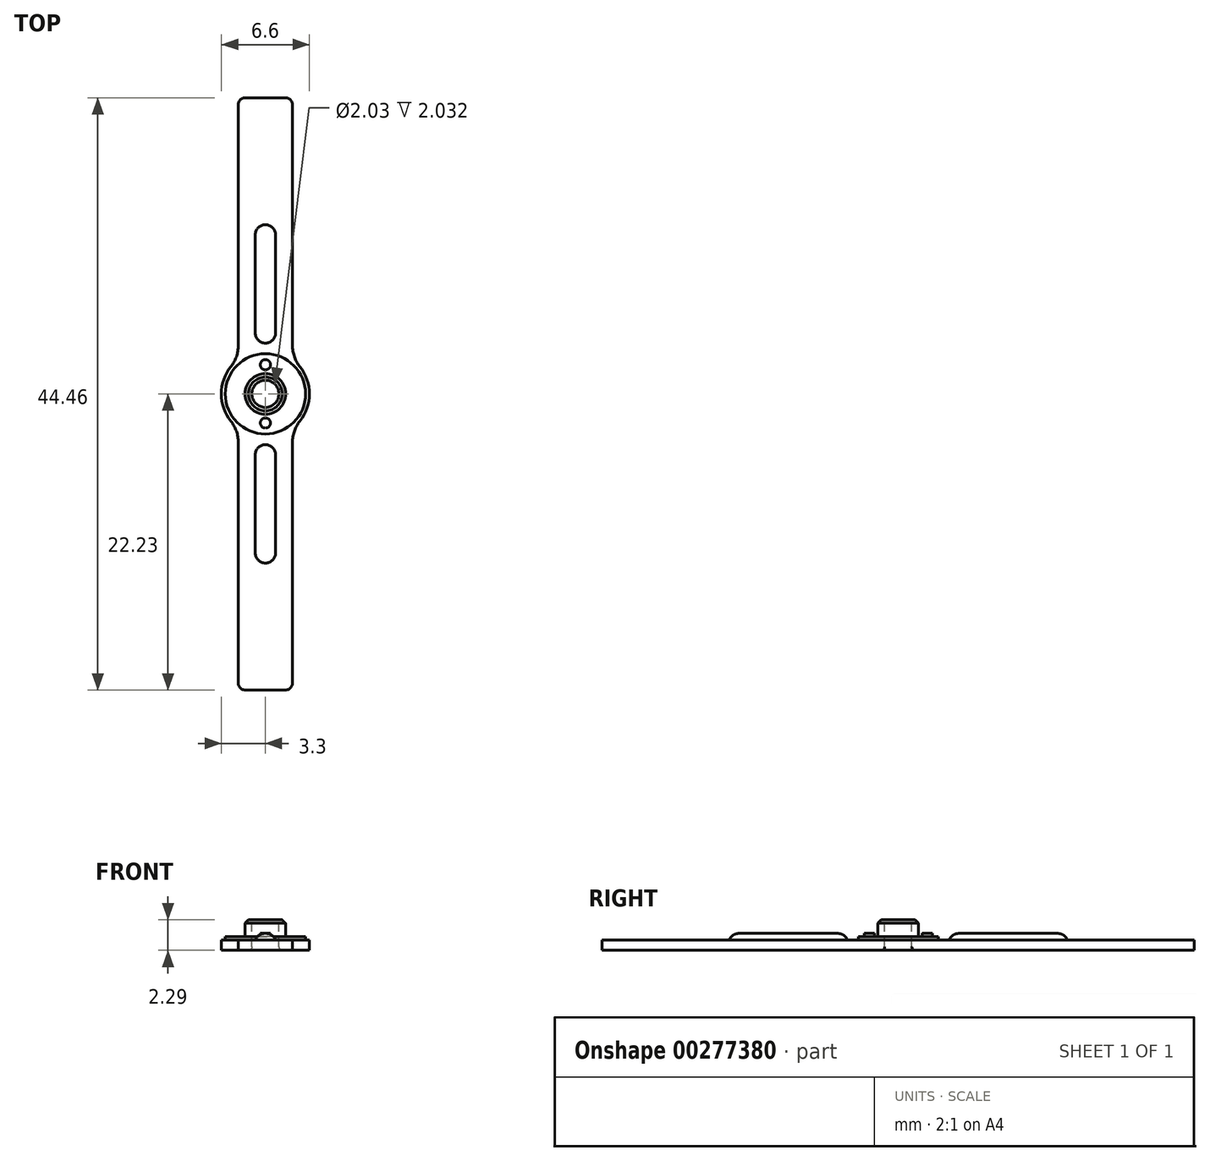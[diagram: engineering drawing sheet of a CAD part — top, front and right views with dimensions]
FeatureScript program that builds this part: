
annotation { "Feature Type Name" : "Feature", "Feature Type Description" : "" }
export const myFeature = defineFeature(function(context is Context, id is Id, definition is map)
    precondition{}
    {
        {
            var Q0;
            Q0=qCreatedBy(makeId("Top.planeOp"),FACE);
            var sketch = newSketch(context, id + "F0", { "sketchPlane" : qUnion([Q0])});
            skArc(sketch, "E0", {"start": v(2.03, -2.6) * mm, "mid": v(3.3, 0) * mm, "end": v(2.03, 2.6) * mm});
            skLineSegment(sketch, "E1", {"start": v(-2.03, 14.6) * mm, "end": v(-2.03, 2.6) * mm});
            skLineSegment(sketch, "E2", {"start": v(2.03, 14.6) * mm, "end": v(2.03, 2.6) * mm});
            skLineSegment(sketch, "E3", {"start": v(-2.03, 22.22) * mm, "end": v(2.03, 22.22) * mm});
            skLineSegment(sketch, "E4", {"start": v(-2.03, -22.23) * mm, "end": v(2.03, -22.22) * mm});
            skPoint(sketch, "E5.orphan", {"position": v(-2.03, -22.23) * mm});
            skPoint(sketch, "E6.orphan", {"position": v(2.03, -22.22) * mm});
            skArc(sketch, "E7.trimOffspring", {"start": v(-2.03, 2.6) * mm, "mid": v(-3.3, 0) * mm, "end": v(-2.03, -2.6) * mm});
            skLineSegment(sketch, "E8.trimOffspring", {"start": v(-2.03, -2.6) * mm, "end": v(-2.03, -14.6) * mm});
            skLineSegment(sketch, "E9.trimOffspring", {"start": v(2.03, -2.6) * mm, "end": v(2.03, -14.6) * mm});
            skPoint(sketch, "E10.orphan", {"position": v(-2.03, 22.22) * mm});
            skPoint(sketch, "E11.orphan", {"position": v(2.03, 22.23) * mm});
            skLineSegment(sketch, "E12", {"start": v(-2.03, 14.6) * mm, "end": v(-2.03, 22.22) * mm});
            skLineSegment(sketch, "E13", {"start": v(2.03, 14.6) * mm, "end": v(2.03, 22.23) * mm});
            skLineSegment(sketch, "E14", {"start": v(-2.03, -14.6) * mm, "end": v(-2.03, -22.23) * mm});
            skLineSegment(sketch, "E15", {"start": v(2.03, -14.6) * mm, "end": v(2.03, -22.22) * mm});
            skPoint(sketch, "E16.orphan", {"position": v(-5.08, -22.23) * mm});
            skPoint(sketch, "E17.end.orphan", {"position": v(5.08, -22.23) * mm});
            skPoint(sketch, "E18.orphan", {"position": v(-5.08, 22.22) * mm});
            skPoint(sketch, "E19.start.orphan", {"position": v(5.08, 22.22) * mm});
            skSolve(sketch);
        }
        {
            var Q0;
            Q0=qSketchRegion(id+"F0",true);
            extrude(context, id + "F1", {"entities" : qUnion([Q0]), "depth" : 0.76 * mm});
        }
        {
            var Q0;
            Q0=makeQuery(id+"F1.opExtrude","SWEPT_EDGE",EDGE,{"disambiguationData":[OSD([sQuery(id+"F0.wireOp",EDGE,"E1"),sQuery(id+"F0.wireOp",EDGE,"E7.trimOffspring")])]});
            var Q1;
            Q1=makeQuery(id+"F1.opExtrude","SWEPT_EDGE",EDGE,{"disambiguationData":[OSD([sQuery(id+"F0.wireOp",EDGE,"E7.trimOffspring"),sQuery(id+"F0.wireOp",EDGE,"E8.trimOffspring")])]});
            var Q2;
            Q2=makeQuery(id+"F1.opExtrude","SWEPT_EDGE",EDGE,{"disambiguationData":[OSD([sQuery(id+"F0.wireOp",EDGE,"E0"),sQuery(id+"F0.wireOp",EDGE,"E2")])]});
            var Q3;
            Q3=makeQuery(id+"F1.opExtrude","SWEPT_EDGE",EDGE,{"disambiguationData":[OSD([sQuery(id+"F0.wireOp",EDGE,"E0"),sQuery(id+"F0.wireOp",EDGE,"E9.trimOffspring")])]});
            var Q4;
            Q4=makeQuery(id+"F1.opExtrude","SWEPT_EDGE",EDGE,{"disambiguationData":[OSD([sQuery(id+"F0.wireOp",EDGE,"E17"),sQuery(id+"F0.wireOp",EDGE,"E9.trimOffspring")])]});
            var Q5;
            Q5=makeQuery(id+"F1.opExtrude","SWEPT_EDGE",EDGE,{"disambiguationData":[OSD([sQuery(id+"F0.wireOp",EDGE,"f60c2798-4896-41d1-aea5-eeca1c1794b5"),sQuery(id+"F0.wireOp",EDGE,"E8.trimOffspring")])]});
            var Q6;
            Q6=makeQuery(id+"F1.opExtrude","SWEPT_EDGE",EDGE,{"disambiguationData":[OSD([sQuery(id+"F0.wireOp",EDGE,"E1"),sQuery(id+"F0.wireOp",EDGE,"a5238ec0-0865-490b-b89e-782f1740bdfc")])]});
            var Q7;
            Q7=makeQuery(id+"F1.opExtrude","SWEPT_EDGE",EDGE,{"disambiguationData":[OSD([sQuery(id+"F0.wireOp",EDGE,"E2"),sQuery(id+"F0.wireOp",EDGE,"E19")])]});
            fillet(context, id + "F2", {"entities" : qUnion([Q0, Q1, Q2, Q3, Q4, Q5, Q6, Q7]), "radius" : 2.54 * mm, "tangentPropagation" : true, "allowEdgeOverflow" : false});
        }
        {
            var Q0;
            Q0=makeQuery(id+"F1.opExtrude","SWEPT_EDGE",EDGE,{"disambiguationData":[OSD([sQuery(id+"F0.wireOp",EDGE,"E3"),sQuery(id+"F0.wireOp",EDGE,"a5238ec0-0865-490b-b89e-782f1740bdfc")])]});
            var Q1;
            Q1=makeQuery(id+"F1.opExtrude","SWEPT_EDGE",EDGE,{"disambiguationData":[OSD([sQuery(id+"F0.wireOp",EDGE,"E3"),sQuery(id+"F0.wireOp",EDGE,"E19")])]});
            var Q2;
            Q2=makeQuery(id+"F1.opExtrude","SWEPT_EDGE",EDGE,{"disambiguationData":[OSD([sQuery(id+"F0.wireOp",EDGE,"E4"),sQuery(id+"F0.wireOp",EDGE,"E17")])]});
            var Q3;
            Q3=makeQuery(id+"F1.opExtrude","SWEPT_EDGE",EDGE,{"disambiguationData":[OSD([sQuery(id+"F0.wireOp",EDGE,"E4"),sQuery(id+"F0.wireOp",EDGE,"f60c2798-4896-41d1-aea5-eeca1c1794b5")])]});
            fillet(context, id + "F3", {"entities" : qUnion([Q0, Q1, Q2, Q3]), "radius" : 0.5 * mm, "tangentPropagation" : true, "allowEdgeOverflow" : false});
        }
        {
            var Q0;
            Q0=makeQuery(id+"F1.opExtrude","CAP_FACE",FACE,{"disambiguationData":[OSD([sQuery(id+"F0.wireOp",EDGE,"E0"),sQuery(id+"F0.wireOp",EDGE,"E1"),sQuery(id+"F0.wireOp",EDGE,"E2"),sQuery(id+"F0.wireOp",EDGE,"E3"),sQuery(id+"F0.wireOp",EDGE,"E4"),sQuery(id+"F0.wireOp",EDGE,"a5238ec0-0865-490b-b89e-782f1740bdfc"),sQuery(id+"F0.wireOp",EDGE,"E19"),sQuery(id+"F0.wireOp",EDGE,"f60c2798-4896-41d1-aea5-eeca1c1794b5"),sQuery(id+"F0.wireOp",EDGE,"E17"),sQuery(id+"F0.wireOp",EDGE,"E7.trimOffspring"),sQuery(id+"F0.wireOp",EDGE,"E8.trimOffspring"),sQuery(id+"F0.wireOp",EDGE,"E9.trimOffspring")])],"isStart":false});
            var sketch = newSketch(context, id + "F4", { "sketchPlane" : qUnion([Q0])});
            skCircle(sketch, "E20", {"center": v(0, 0) * mm, "radius": 3.01 * mm});
            skSolve(sketch);
        }
        {
            var Q0;
            Q0=qSketchRegion(id+"F4",true);
            extrude(context, id + "F5", {"entities" : qUnion([Q0]), "operationType" : NewBodyOperationType.ADD, "depth" : 0.25 * mm});
        }
        {
            var Q0;
            Q0=makeQuery(id+"F5.opExtrude","CAP_FACE",FACE,{"disambiguationData":[OSD([sQuery(id+"F4.wireOp",EDGE,"E20")])],"isStart":false});
            var sketch = newSketch(context, id + "F6", { "sketchPlane" : qUnion([Q0])});
            skCircle(sketch, "E21", {"center": v(0, 0) * mm, "radius": 1.52 * mm});
            skSolve(sketch);
        }
        {
            var Q0;
            Q0=qSketchRegion(id+"F6",true);
            extrude(context, id + "F7", {"entities" : qUnion([Q0]), "operationType" : NewBodyOperationType.ADD, "depth" : 1.27 * mm});
        }
        {
            var Q0;
            Q0=makeQuery(id+"F7.opExtrude","CAP_EDGE",EDGE,{"disambiguationData":[OSD([sQuery(id+"F6.wireOp",EDGE,"E21")])],"isStart":false});
            chamfer(context, id + "F8", {"entities" : qUnion([Q0]), "width" : 0.25 * mm, "tangentPropagation" : true});
        }
        {
            var Q0;
            Q0=makeQuery(id+"F5.opExtrude","CAP_FACE",FACE,{"disambiguationData":[OSD([sQuery(id+"F4.wireOp",EDGE,"E20")])],"isStart":false});
            var sketch = newSketch(context, id + "F9", { "sketchPlane" : qUnion([Q0])});
            skCircle(sketch, "E22", {"center": v(0, 2.18) * mm, "radius": 0.38 * mm});
            skCircle(sketch, "E23", {"center": v(0, -2.18) * mm, "radius": 0.38 * mm});
            skSolve(sketch);
        }
        {
            var Q0;
            Q0=qSketchRegion(id+"F9",true);
            extrude(context, id + "F10", {"entities" : qUnion([Q0]), "operationType" : NewBodyOperationType.ADD, "depth" : 0.25 * mm});
        }
        {
            var Q0;
            Q0=makeQuery(id+"F7.opExtrude","CAP_FACE",FACE,{"disambiguationData":[OSD([sQuery(id+"F6.wireOp",EDGE,"E21")])],"isStart":false});
            var sketch = newSketch(context, id + "F11", { "sketchPlane" : qUnion([Q0])});
            skCircle(sketch, "E24", {"center": v(0, 0) * mm, "radius": 1.02 * mm});
            skSolve(sketch);
        }
        {
            var Q0;
            Q0=qSketchRegion(id+"F11",true);
            extrude(context, id + "F12", {"entities" : qUnion([Q0]), "operationType" : NewBodyOperationType.REMOVE, "oppositeDirection" : true, "depth" : 25.4 * mm});
        }
        {
            var Q0;
            Q0=makeQuery(id+"F12.boolean.opBoolean","COPY",EDGE,{"derivedFrom":makeQuery(id+"F12.opExtrude","CAP_EDGE",EDGE,{"disambiguationData":[OSD([sQuery(id+"F11.wireOp",EDGE,"E24")])],"isStart":true})});
            var Q1;
            Q1=makeQuery(id+"F12.boolean.opBoolean","INTERSECT",EDGE,{"derivedFrom":[makeQuery(id+"F1.opExtrude","CAP_FACE",FACE,{"disambiguationData":[OSD([sQuery(id+"F0.wireOp",EDGE,"E0"),sQuery(id+"F0.wireOp",EDGE,"E1"),sQuery(id+"F0.wireOp",EDGE,"E2"),sQuery(id+"F0.wireOp",EDGE,"E3"),sQuery(id+"F0.wireOp",EDGE,"E4"),sQuery(id+"F0.wireOp",EDGE,"a5238ec0-0865-490b-b89e-782f1740bdfc"),sQuery(id+"F0.wireOp",EDGE,"E19"),sQuery(id+"F0.wireOp",EDGE,"f60c2798-4896-41d1-aea5-eeca1c1794b5"),sQuery(id+"F0.wireOp",EDGE,"E17"),sQuery(id+"F0.wireOp",EDGE,"E7.trimOffspring"),sQuery(id+"F0.wireOp",EDGE,"E8.trimOffspring"),sQuery(id+"F0.wireOp",EDGE,"E9.trimOffspring")])],"isStart":true}),makeQuery(id+"F12.opExtrude","SWEPT_FACE",FACE,{"disambiguationData":[OSD([sQuery(id+"F11.wireOp",EDGE,"E24")])]})]});
            fillet(context, id + "F13", {"entities" : qUnion([Q0, Q1]), "radius" : 0.25 * mm, "tangentPropagation" : true, "allowEdgeOverflow" : false});
        }
        {
            var Q0;
            Q0=makeQuery(id+"F1.opExtrude","CAP_FACE",FACE,{"disambiguationData":[OSD([sQuery(id+"F0.wireOp",EDGE,"E0"),sQuery(id+"F0.wireOp",EDGE,"E1"),sQuery(id+"F0.wireOp",EDGE,"E2"),sQuery(id+"F0.wireOp",EDGE,"E3"),sQuery(id+"F0.wireOp",EDGE,"E4"),sQuery(id+"F0.wireOp",EDGE,"a5238ec0-0865-490b-b89e-782f1740bdfc"),sQuery(id+"F0.wireOp",EDGE,"E19"),sQuery(id+"F0.wireOp",EDGE,"f60c2798-4896-41d1-aea5-eeca1c1794b5"),sQuery(id+"F0.wireOp",EDGE,"E17"),sQuery(id+"F0.wireOp",EDGE,"E7.trimOffspring"),sQuery(id+"F0.wireOp",EDGE,"E8.trimOffspring"),sQuery(id+"F0.wireOp",EDGE,"E9.trimOffspring")])],"isStart":false});
            var sketch = newSketch(context, id + "F14", { "sketchPlane" : qUnion([Q0])});
            skLineSegment(sketch, "E25.bottom", {"start": v(0, 12.7) * mm, "end": v(0, 12.7) * mm});
            skLineSegment(sketch, "E25.top", {"start": v(0, 3.81) * mm, "end": v(0, 3.81) * mm});
            skLineSegment(sketch, "E25.left", {"start": v(-0.76, 11.94) * mm, "end": v(-0.76, 4.57) * mm});
            skLineSegment(sketch, "E25.right", {"start": v(0.76, 11.94) * mm, "end": v(0.76, 4.57) * mm});
            skLineSegment(sketch, "E26.bottom", {"start": v(0, -3.81) * mm, "end": v(0, -3.81) * mm});
            skLineSegment(sketch, "E26.top", {"start": v(0, -12.7) * mm, "end": v(0, -12.7) * mm});
            skLineSegment(sketch, "E26.left", {"start": v(-0.76, -4.57) * mm, "end": v(-0.76, -11.94) * mm});
            skLineSegment(sketch, "E26.right", {"start": v(0.76, -4.57) * mm, "end": v(0.76, -11.94) * mm});
            skPoint(sketch, "E27.visualSharp", {"position": v(-0.76, -3.81) * mm});
            skArc(sketch, "E27.filletArc", {"start": v(0, -3.81) * mm, "mid": v(-0.54, -4.03) * mm, "end": v(-0.76, -4.57) * mm});
            skPoint(sketch, "E28.visualSharp", {"position": v(0.76, -3.81) * mm});
            skArc(sketch, "E28.filletArc", {"start": v(0.76, -4.57) * mm, "mid": v(0.54, -4.03) * mm, "end": v(0, -3.81) * mm});
            skPoint(sketch, "E29.visualSharp", {"position": v(-0.76, -12.7) * mm});
            skArc(sketch, "E29.filletArc", {"start": v(-0.76, -11.94) * mm, "mid": v(-0.54, -12.48) * mm, "end": v(0, -12.7) * mm});
            skPoint(sketch, "E30.visualSharp", {"position": v(0.76, -12.7) * mm});
            skArc(sketch, "E30.filletArc", {"start": v(0, -12.7) * mm, "mid": v(0.54, -12.48) * mm, "end": v(0.76, -11.94) * mm});
            skPoint(sketch, "E31.visualSharp", {"position": v(0.76, 3.81) * mm});
            skArc(sketch, "E31.filletArc", {"start": v(0, 3.81) * mm, "mid": v(0.54, 4.03) * mm, "end": v(0.76, 4.57) * mm});
            skPoint(sketch, "E32.visualSharp", {"position": v(-0.76, 3.81) * mm});
            skArc(sketch, "E32.filletArc", {"start": v(-0.76, 4.57) * mm, "mid": v(-0.54, 4.03) * mm, "end": v(0, 3.81) * mm});
            skPoint(sketch, "E33.visualSharp", {"position": v(-0.76, 12.7) * mm});
            skArc(sketch, "E33.filletArc", {"start": v(0, 12.7) * mm, "mid": v(-0.54, 12.48) * mm, "end": v(-0.76, 11.94) * mm});
            skPoint(sketch, "E34.visualSharp", {"position": v(0.76, 12.7) * mm});
            skArc(sketch, "E34.filletArc", {"start": v(0.76, 11.94) * mm, "mid": v(0.54, 12.48) * mm, "end": v(0, 12.7) * mm});
            skSolve(sketch);
        }
        {
            var Q0;
            Q0=qSketchRegion(id+"F14",true);
            extrude(context, id + "F15", {"entities" : qUnion([Q0]), "operationType" : NewBodyOperationType.ADD, "depth" : 0.5 * mm});
        }
        {
            var Q0;
            Q0=makeQuery(id+"F15.opExtrude","CAP_FACE",FACE,{"disambiguationData":[OSD([sQuery(id+"F14.wireOp",EDGE,"E25.left"),sQuery(id+"F14.wireOp",EDGE,"E25.right"),sQuery(id+"F14.wireOp",EDGE,"E31.filletArc"),sQuery(id+"F14.wireOp",EDGE,"E32.filletArc"),sQuery(id+"F14.wireOp",EDGE,"E33.filletArc"),sQuery(id+"F14.wireOp",EDGE,"E34.filletArc")])],"isStart":false});
            var Q1;
            Q1=makeQuery(id+"F15.opExtrude","CAP_FACE",FACE,{"disambiguationData":[OSD([sQuery(id+"F14.wireOp",EDGE,"E26.left"),sQuery(id+"F14.wireOp",EDGE,"E26.right"),sQuery(id+"F14.wireOp",EDGE,"E27.filletArc"),sQuery(id+"F14.wireOp",EDGE,"E28.filletArc"),sQuery(id+"F14.wireOp",EDGE,"E29.filletArc"),sQuery(id+"F14.wireOp",EDGE,"E30.filletArc")])],"isStart":false});
            fillet(context, id + "F16", {"entities" : qUnion([Q0, Q1]), "radius" : 0.76 * mm, "tangentPropagation" : true, "allowEdgeOverflow" : false});
        }
    });
